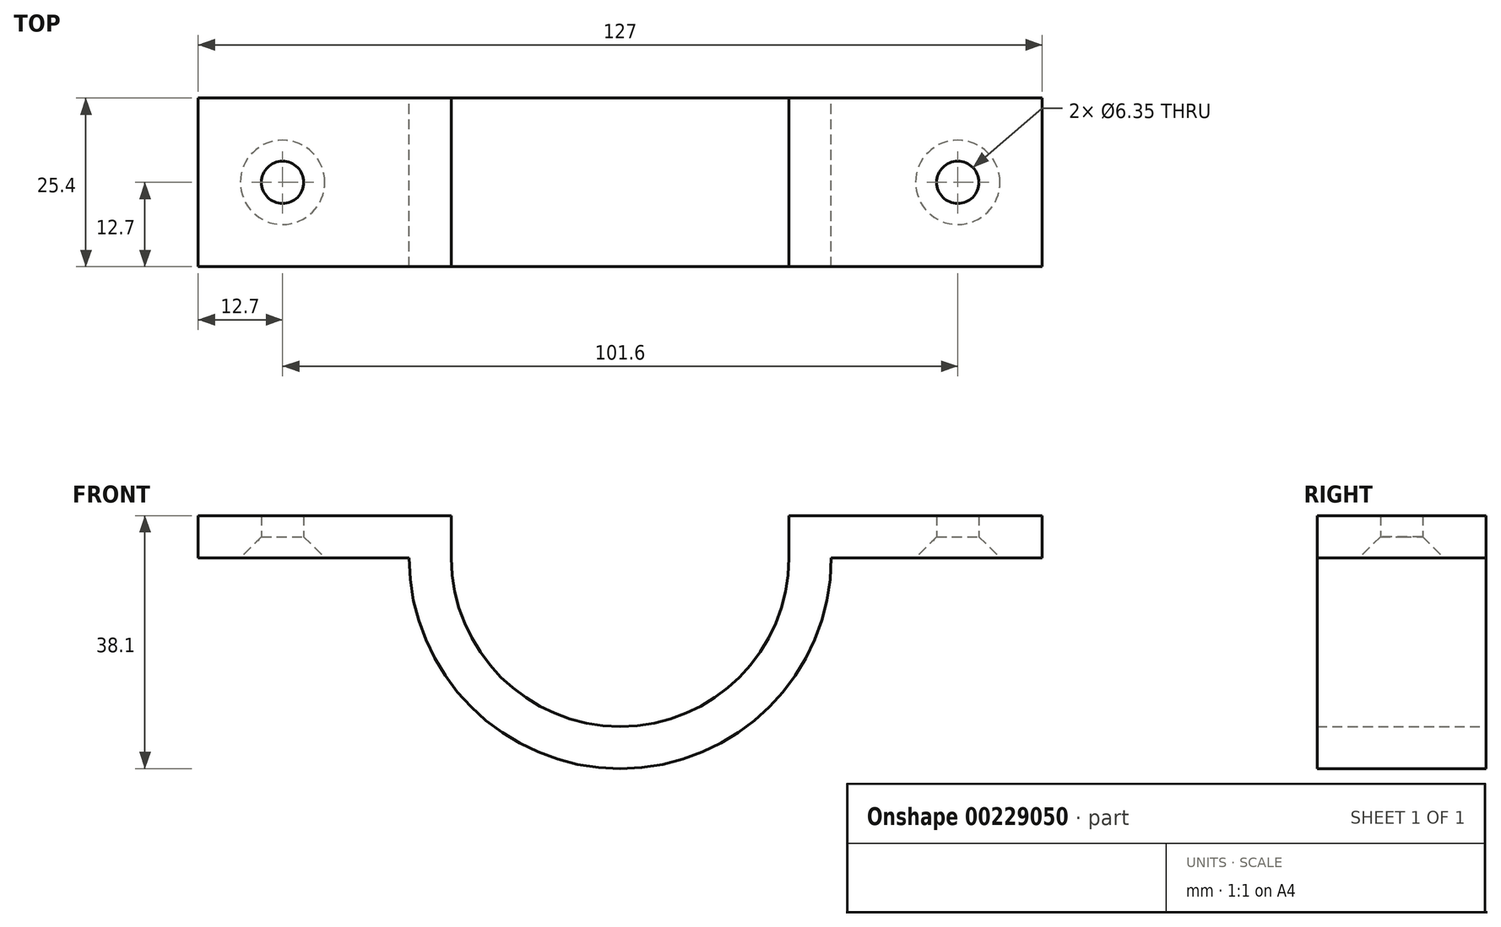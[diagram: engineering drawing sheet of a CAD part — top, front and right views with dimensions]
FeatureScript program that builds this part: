
annotation { "Feature Type Name" : "Feature", "Feature Type Description" : "" }
export const myFeature = defineFeature(function(context is Context, id is Id, definition is map)
    precondition{}
    {
        {
            var Q0;
            Q0=qCreatedBy(makeId("Front.planeOp"),FACE);
            var sketch = newSketch(context, id + "F0", { "sketchPlane" : qUnion([Q0])});
            skArc(sketch, "E0", {"start": v(0, -25.4) * mm, "mid": v(17.96, -17.96) * mm, "end": v(25.4, 0) * mm});
            skArc(sketch, "E1.0", {"start": v(0, -31.75) * mm, "mid": v(22.45, -22.45) * mm, "end": v(31.75, 0) * mm});
            skArc(sketch, "E2", {"start": v(0, -25.4) * mm, "mid": v(-17.96, -17.96) * mm, "end": v(-25.4, 0) * mm});
            skArc(sketch, "E3.0", {"start": v(0, -31.75) * mm, "mid": v(-22.45, -22.45) * mm, "end": v(-31.75, 0) * mm});
            skLineSegment(sketch, "E4.bottom", {"start": v(-25.4, 0) * mm, "end": v(-63.5, 0) * mm});
            skLineSegment(sketch, "E4.top", {"start": v(-25.4, 6.35) * mm, "end": v(-63.5, 6.35) * mm});
            skLineSegment(sketch, "E4.left", {"start": v(-25.4, 0) * mm, "end": v(-25.4, 6.35) * mm});
            skLineSegment(sketch, "E4.right", {"start": v(-63.5, 0) * mm, "end": v(-63.5, 6.35) * mm});
            skLineSegment(sketch, "E5.bottom", {"start": v(25.4, 0) * mm, "end": v(63.5, 0) * mm});
            skLineSegment(sketch, "E5.top", {"start": v(25.4, 6.35) * mm, "end": v(63.5, 6.35) * mm});
            skLineSegment(sketch, "E5.left", {"start": v(25.4, 0) * mm, "end": v(25.4, 6.35) * mm});
            skLineSegment(sketch, "E5.right", {"start": v(63.5, 0) * mm, "end": v(63.5, 6.35) * mm});
            skSolve(sketch);
        }
        {
            var Q0;
            {var subQ3=sQuery(id+"F0.wireOp",EDGE,"E0");Q0=makeQuery(id+"F0.imprint","IMPRINT",FACE,{"disambiguationData":[TD([[makeQuery(id+"F0.imprint","IMPRINT",EDGE,{"derivedFrom":subQ3}),-1.0]])]});}
            var Q1;
            Q1=makeQuery(id+"F0.imprint","IMPRINT",FACE,{"disambiguationData":[TD([[makeQuery(id+"F0.imprint","IMPRINT",EDGE,{"derivedFrom":sQuery(id+"F0.wireOp",EDGE,"E4.top")}),1.0]])]});
            var Q2;
            Q2=makeQuery(id+"F0.imprint","IMPRINT",FACE,{"disambiguationData":[TD([[makeQuery(id+"F0.imprint","IMPRINT",EDGE,{"derivedFrom":sQuery(id+"F0.wireOp",EDGE,"E5.top")}),-1.0]])]});
            extrude(context, id + "F1", {"entities" : qUnion([Q0, Q1, Q2]), "endBound" : BoundingType.SYMMETRIC, "depth" : 25.4 * mm});
        }
        {
            var Q0;
            Q0=qCreatedBy(makeId("Top.planeOp"),FACE);
            var sketch = newSketch(context, id + "F2", { "sketchPlane" : qUnion([Q0])});
            skCircle(sketch, "E6", {"center": v(50.8, 0) * mm, "radius": 3.18 * mm});
            skCircle(sketch, "E7", {"center": v(-50.8, 0) * mm, "radius": 3.18 * mm});
            skSolve(sketch);
        }
        {
            var Q0;
            Q0=sQuery(id+"F2.wireOp",VERTEX,"E7.center");
            var Q1;
            Q1=sQuery(id+"F2.wireOp",VERTEX,"E6.center");
            var Q2;
            Q2=makeQuery(id+"F1.opExtrude","SWEPT_BODY",BODY,{"disambiguationData":[OSD([sQuery(id+"F0.wireOp",EDGE,"E0"),sQuery(id+"F0.wireOp",EDGE,"E1.0"),sQuery(id+"F0.wireOp",EDGE,"E2"),sQuery(id+"F0.wireOp",EDGE,"E3.0"),sQuery(id+"F0.wireOp",EDGE,"E4.bottom"),sQuery(id+"F0.wireOp",EDGE,"E4.top"),sQuery(id+"F0.wireOp",EDGE,"E4.left"),sQuery(id+"F0.wireOp",EDGE,"E4.right"),sQuery(id+"F0.wireOp",EDGE,"E5.bottom"),sQuery(id+"F0.wireOp",EDGE,"E5.top"),sQuery(id+"F0.wireOp",EDGE,"E5.left"),sQuery(id+"F0.wireOp",EDGE,"E5.right")])]});
            hole(context, id + "F3", {"style" : HoleStyle.C_SINK, "endStyle" : HoleEndStyle.THROUGH, "oppositeDirection" : true, "holeDiameter" : 6.35 * mm, "cSinkDiameter" : 12.7 * mm, "cSinkAngle" : 90 * degree, "locations" : qUnion([Q0, Q1]), "scope" : qUnion([Q2]), "isTappedThrough" : true});
        }
    });
